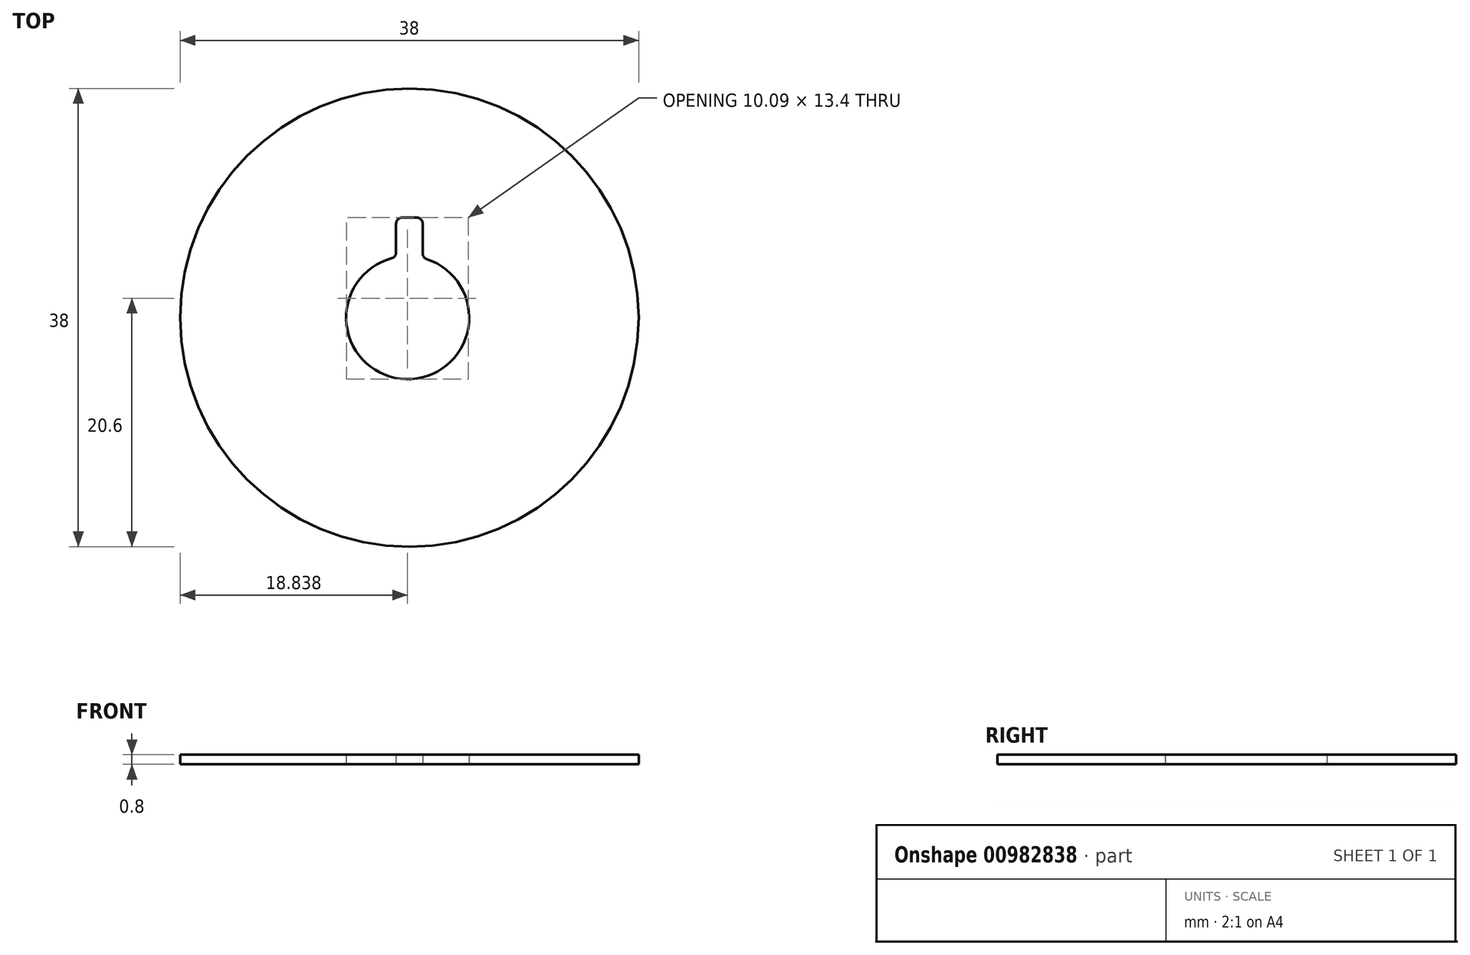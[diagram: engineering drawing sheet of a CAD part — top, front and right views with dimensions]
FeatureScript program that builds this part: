
annotation { "Feature Type Name" : "Feature", "Feature Type Description" : "" }
export const myFeature = defineFeature(function(context is Context, id is Id, definition is map)
    precondition{}
    {
        {
            var Q0;
            Q0=qCreatedBy(makeId("Top.planeOp"),FACE);
            var sketch = newSketch(context, id + "F0", { "sketchPlane" : qUnion([Q0])});
            skCircle(sketch, "E0", {"center": v(0, 0) * mm, "radius": 19 * mm});
            skCircle(sketch, "E1", {"center": v(-0.14, 0) * mm, "radius": 5.1 * mm});
            skLineSegment(sketch, "E2", {"start": v(0, 5.1) * mm, "end": v(0, 8.3) * mm, "construction": true});
            skLineSegment(sketch, "E3", {"start": v(-1.1, 8.3) * mm, "end": v(1.1, 8.3) * mm});
            skLineSegment(sketch, "E4", {"start": v(-1.1, 8.3) * mm, "end": v(-1.1, 5) * mm});
            skLineSegment(sketch, "E5", {"start": v(1.1, 8.3) * mm, "end": v(1.1, 4.95) * mm});
            skSolve(sketch);
        }
        {
            var Q0;
            Q0=makeQuery(id+"F0.imprint","IMPRINT",FACE,{"disambiguationData":[TD([[makeQuery(id+"F0.imprint","IMPRINT",EDGE,{"derivedFrom":sQuery(id+"F0.wireOp",EDGE,"E0")}),1.0]])]});
            extrude(context, id + "F1", {"entities" : qUnion([Q0]), "depth" : 0.8 * mm, "offsetDistance" : 25 * mm});
        }
        {
            var Q0;
            Q0=makeQuery(id+"F1.opExtrude","SWEPT_EDGE",EDGE,{"disambiguationData":[OSD([sQuery(id+"F0.wireOp",EDGE,"E1"),sQuery(id+"F0.wireOp",EDGE,"E5")])]});
            var Q1;
            Q1=makeQuery(id+"F1.opExtrude","SWEPT_EDGE",EDGE,{"disambiguationData":[OSD([sQuery(id+"F0.wireOp",EDGE,"E3"),sQuery(id+"F0.wireOp",EDGE,"E5")])]});
            var Q2;
            Q2=makeQuery(id+"F1.opExtrude","SWEPT_EDGE",EDGE,{"disambiguationData":[OSD([sQuery(id+"F0.wireOp",EDGE,"E3"),sQuery(id+"F0.wireOp",EDGE,"E4")])]});
            var Q3;
            Q3=makeQuery(id+"F1.opExtrude","SWEPT_EDGE",EDGE,{"disambiguationData":[OSD([sQuery(id+"F0.wireOp",EDGE,"E1"),sQuery(id+"F0.wireOp",EDGE,"E4")])]});
            fillet(context, id + "F2", {"entities" : qUnion([Q0, Q1, Q2, Q3]), "radius" : 0.5 * mm, "tangentPropagation" : true, "allowEdgeOverflow" : false});
        }
    });
